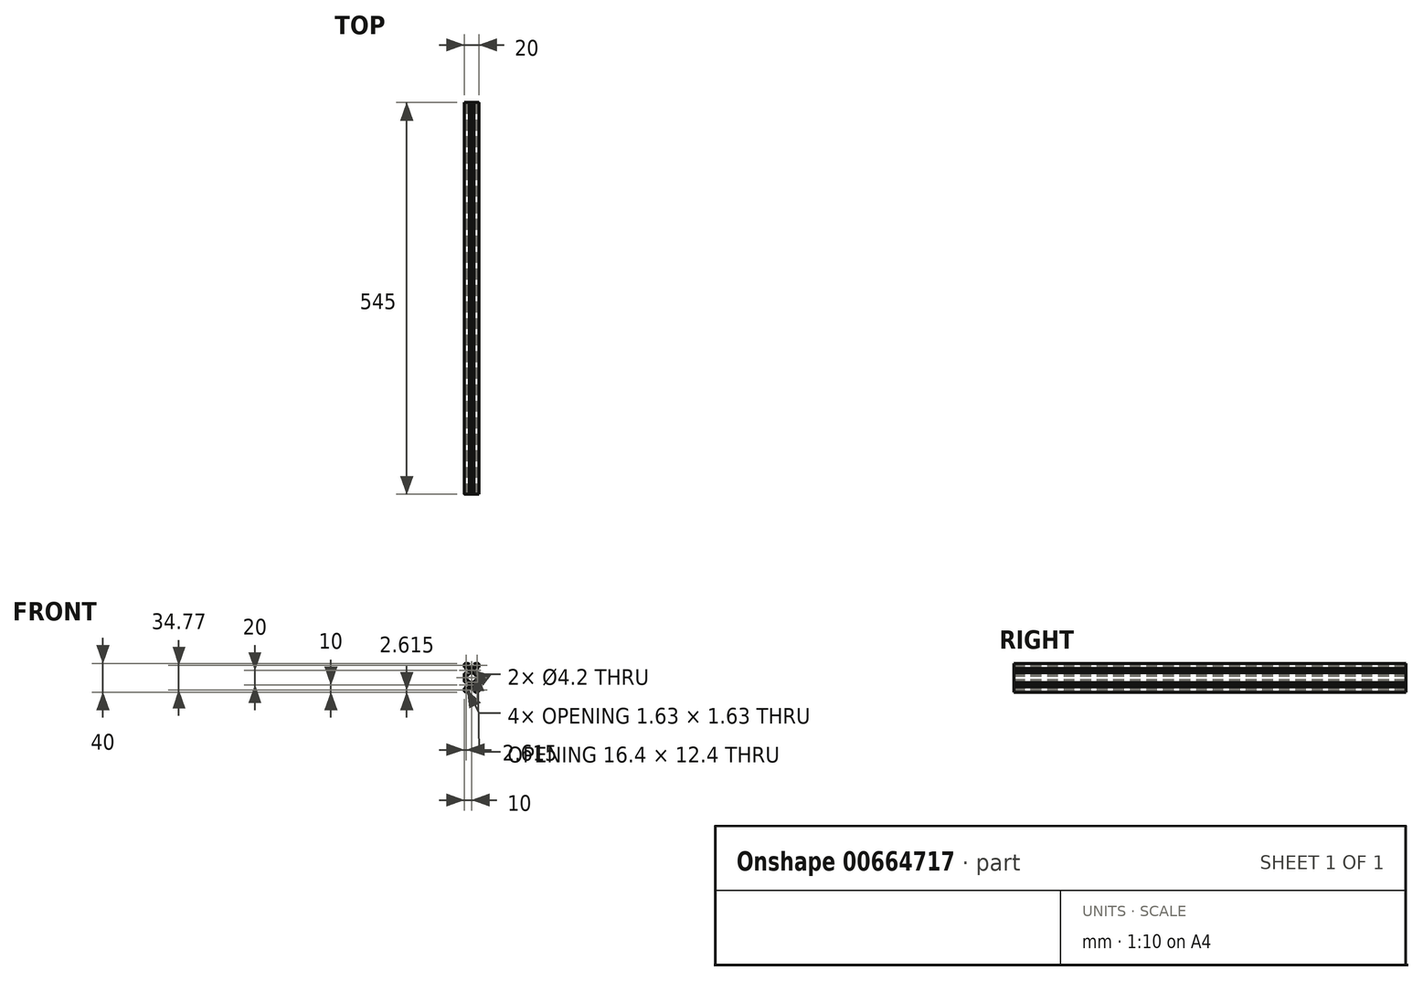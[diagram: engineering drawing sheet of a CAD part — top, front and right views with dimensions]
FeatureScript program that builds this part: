
annotation { "Feature Type Name" : "Feature", "Feature Type Description" : "" }
export const myFeature = defineFeature(function(context is Context, id is Id, definition is map)
    precondition{}
    {
        {
            var Q0;
            Q0=qCreatedBy(makeId("Front.planeOp"),FACE);
            var sketch = newSketch(context, id + "F0", { "sketchPlane" : qUnion([Q0])});
            skLineSegment(sketch, "E0", {"start": v(1.5, 0) * mm, "end": v(5.1, 0) * mm});
            skLineSegment(sketch, "E1", {"start": v(0, -1.5) * mm, "end": v(0, -5.1) * mm});
            skLineSegment(sketch, "E2", {"start": v(5.65, -0.23) * mm, "end": v(7.11, -1.69) * mm});
            skLineSegment(sketch, "E3", {"start": v(7.11, -1.7) * mm, "end": v(7.11, -1.8) * mm});
            skLineSegment(sketch, "E4", {"start": v(0.23, -5.65) * mm, "end": v(1.69, -7.11) * mm});
            skLineSegment(sketch, "E5", {"start": v(1.7, -7.11) * mm, "end": v(1.8, -7.11) * mm});
            skLineSegment(sketch, "E6", {"start": v(1.8, -7.11) * mm, "end": v(1.8, -4.5) * mm});
            skLineSegment(sketch, "E7", {"start": v(1.8, -4.5) * mm, "end": v(3.44, -4.5) * mm});
            skLineSegment(sketch, "E8", {"start": v(7.11, -1.8) * mm, "end": v(4.5, -1.8) * mm});
            skLineSegment(sketch, "E9", {"start": v(4.5, -1.8) * mm, "end": v(4.5, -3.44) * mm});
            skPoint(sketch, "E10.visualSharp", {"position": v(0, 0) * mm});
            skArc(sketch, "E10.filletArc", {"start": v(1.5, 0) * mm, "mid": v(0.44, -0.44) * mm, "end": v(0, -1.5) * mm});
            skPoint(sketch, "E11.visualSharp", {"position": v(5.42, 0) * mm});
            skArc(sketch, "E11.filletArc", {"start": v(5.65, -0.23) * mm, "mid": v(5.4, -0.06) * mm, "end": v(5.1, 0) * mm});
            skPoint(sketch, "E12.visualSharp", {"position": v(0, -5.42) * mm});
            skArc(sketch, "E12.filletArc", {"start": v(0, -5.1) * mm, "mid": v(0.06, -5.4) * mm, "end": v(0.23, -5.65) * mm});
            skLineSegment(sketch, "E13", {"start": v(1.8, -4.5) * mm, "end": v(1.8, 0) * mm, "construction": true});
            skLineSegment(sketch, "E14", {"start": v(4.5, -1.8) * mm, "end": v(0, -1.8) * mm, "construction": true});
            skPoint(sketch, "E15", {"position": v(1.8, -1.8) * mm});
            skLineSegment(sketch, "E16", {"start": v(1.8, -1.8) * mm, "end": v(3.43, -1.8) * mm});
            skLineSegment(sketch, "E17", {"start": v(3.43, -1.8) * mm, "end": v(3.43, -2.34) * mm});
            skLineSegment(sketch, "E18", {"start": v(1.8, -1.8) * mm, "end": v(1.8, -3.43) * mm});
            skLineSegment(sketch, "E19", {"start": v(1.8, -3.43) * mm, "end": v(2.34, -3.43) * mm});
            skLineSegment(sketch, "E20", {"start": v(2.34, -3.43) * mm, "end": v(3.43, -2.34) * mm});
            skArc(sketch, "E21", {"start": v(10, -7.9) * mm, "mid": v(8.52, -8.52) * mm, "end": v(7.9, -10) * mm});
            skLineSegment(sketch, "E22", {"start": v(10, -7.9) * mm, "end": v(10, -6.2) * mm, "construction": true});
            skLineSegment(sketch, "E23", {"start": v(9.9, -6.1) * mm, "end": v(7.16, -6.1) * mm});
            skLineSegment(sketch, "E24", {"start": v(7.16, -6.1) * mm, "end": v(4.5, -3.44) * mm});
            skLineSegment(sketch, "E25", {"start": v(7.9, -10) * mm, "end": v(6.2, -10) * mm, "construction": true});
            skLineSegment(sketch, "E26", {"start": v(6.1, -9.9) * mm, "end": v(6.1, -7.16) * mm});
            skLineSegment(sketch, "E27", {"start": v(6.1, -7.16) * mm, "end": v(3.44, -4.5) * mm});
            skLineSegment(sketch, "E28", {"start": v(1.8, -1.8) * mm, "end": v(10, -10) * mm, "construction": true});
            skLineSegment(sketch, "E29", {"start": v(6.2, -10) * mm, "end": v(6.1, -9.9) * mm});
            skLineSegment(sketch, "E30", {"start": v(10, -6.2) * mm, "end": v(9.9, -6.1) * mm});
            skArc(sketch, "E31", {"start": v(7.9, -10) * mm, "mid": v(8.52, -11.48) * mm, "end": v(10, -12.1) * mm});
            skLineSegment(sketch, "E32", {"start": v(6.2, -10) * mm, "end": v(6.1, -10.1) * mm});
            skLineSegment(sketch, "E33", {"start": v(6.1, -10.1) * mm, "end": v(6.1, -12.84) * mm});
            skLineSegment(sketch, "E34", {"start": v(10, -12.1) * mm, "end": v(10, -13.8) * mm, "construction": true});
            skLineSegment(sketch, "E35", {"start": v(10, -13.8) * mm, "end": v(9.9, -13.9) * mm});
            skLineSegment(sketch, "E36", {"start": v(9.9, -13.9) * mm, "end": v(7.16, -13.9) * mm});
            skLineSegment(sketch, "E37", {"start": v(6.1, -12.84) * mm, "end": v(7.16, -13.9) * mm, "construction": true});
            skLineSegment(sketch, "E38", {"start": v(7.16, -6.1) * mm, "end": v(6.1, -7.16) * mm, "construction": true});
            skLineSegment(sketch, "E39", {"start": v(6.1, -12.84) * mm, "end": v(3.44, -15.5) * mm});
            skLineSegment(sketch, "E40", {"start": v(7.16, -13.9) * mm, "end": v(3.76, -17.3) * mm});
            skLineSegment(sketch, "E41", {"start": v(10, -10) * mm, "end": v(1.8, -18.2) * mm, "construction": true});
            skLineSegment(sketch, "E42", {"start": v(3.44, -15.5) * mm, "end": v(1.8, -15.5) * mm});
            skLineSegment(sketch, "E43", {"start": v(1.8, -15.5) * mm, "end": v(1.8, -12.89) * mm});
            skLineSegment(sketch, "E44", {"start": v(1.8, -12.89) * mm, "end": v(1.7, -12.89) * mm});
            skLineSegment(sketch, "E45", {"start": v(1.7, -12.89) * mm, "end": v(0.23, -14.35) * mm});
            skLineSegment(sketch, "E46", {"start": v(0, -14.9) * mm, "end": v(0, -20) * mm});
            skLineSegment(sketch, "E47", {"start": v(0, -20) * mm, "end": v(1.8, -20) * mm, "construction": true});
            skLineSegment(sketch, "E48", {"start": v(1.8, -20) * mm, "end": v(1.8, -17.3) * mm});
            skLineSegment(sketch, "E49", {"start": v(1.8, -17.3) * mm, "end": v(3.76, -17.3) * mm});
            skPoint(sketch, "E50.visualSharp", {"position": v(0, -14.58) * mm});
            skArc(sketch, "E50.filletArc", {"start": v(0.23, -14.35) * mm, "mid": v(0.06, -14.6) * mm, "end": v(0, -14.9) * mm});
            skLineSegment(sketch, "E51.MirrorCS", {"start": v(13.8, -10) * mm, "end": v(13.9, -10.1) * mm});
            skLineSegment(sketch, "E52.MirrorCS", {"start": v(13.8, -10) * mm, "end": v(13.9, -9.9) * mm});
            skLineSegment(sketch, "E53.MirrorCS", {"start": v(12.9, -1.69) * mm, "end": v(12.9, -1.8) * mm});
            skLineSegment(sketch, "E54.MirrorCS", {"start": v(16.57, -1.8) * mm, "end": v(16.57, -2.34) * mm});
            skLineSegment(sketch, "E55.MirrorCS", {"start": v(10, -13.8) * mm, "end": v(10.1, -13.9) * mm});
            skLineSegment(sketch, "E56.MirrorCS", {"start": v(12.84, -6.1) * mm, "end": v(13.9, -7.16) * mm, "construction": true});
            skArc(sketch, "E57.MirrorCS", {"start": v(14.35, -0.23) * mm, "mid": v(14.6, -0.06) * mm, "end": v(14.9, 0) * mm});
            skArc(sketch, "E58.MirrorCS", {"start": v(20, -5.1) * mm, "mid": v(19.94, -5.4) * mm, "end": v(19.77, -5.65) * mm});
            skLineSegment(sketch, "E59.MirrorCS", {"start": v(13.9, -12.84) * mm, "end": v(12.84, -13.9) * mm, "construction": true});
            skArc(sketch, "E60.MirrorCS", {"start": v(19.77, -14.35) * mm, "mid": v(19.94, -14.6) * mm, "end": v(20, -14.9) * mm});
            skLineSegment(sketch, "E61.MirrorCS", {"start": v(18.31, -7.11) * mm, "end": v(18.2, -7.11) * mm});
            skLineSegment(sketch, "E62.MirrorCS", {"start": v(10, -6.2) * mm, "end": v(10.1, -6.1) * mm});
            skLineSegment(sketch, "E63.MirrorCS", {"start": v(18.2, -3.43) * mm, "end": v(17.66, -3.43) * mm});
            skLineSegment(sketch, "E64.MirrorCS", {"start": v(18.2, -12.89) * mm, "end": v(18.31, -12.89) * mm});
            skLineSegment(sketch, "E65.MirrorCS", {"start": v(17.66, -3.43) * mm, "end": v(16.57, -2.34) * mm});
            skLineSegment(sketch, "E66.MirrorCS", {"start": v(18.31, -12.89) * mm, "end": v(19.77, -14.35) * mm});
            skLineSegment(sketch, "E67.MirrorCS", {"start": v(18.2, -1.8) * mm, "end": v(16.57, -1.8) * mm});
            skArc(sketch, "E68.MirrorCS", {"start": v(18.5, 0) * mm, "mid": v(19.56, -0.44) * mm, "end": v(20, -1.5) * mm});
            skLineSegment(sketch, "E69.MirrorCS", {"start": v(15.5, -1.8) * mm, "end": v(15.5, -3.44) * mm});
            skLineSegment(sketch, "E70.MirrorCS", {"start": v(12.1, -10) * mm, "end": v(13.8, -10) * mm, "construction": true});
            skLineSegment(sketch, "E71.MirrorCS", {"start": v(18.2, -1.8) * mm, "end": v(18.2, -3.43) * mm});
            skPoint(sketch, "E72.MirrorP", {"position": v(18.2, -1.8) * mm});
            skLineSegment(sketch, "E73.MirrorCS", {"start": v(10.1, -6.1) * mm, "end": v(12.84, -6.1) * mm});
            skLineSegment(sketch, "E74.MirrorCS", {"start": v(20, -20) * mm, "end": v(18.2, -20) * mm, "construction": true});
            skLineSegment(sketch, "E75.MirrorCS", {"start": v(18.2, -7.11) * mm, "end": v(18.2, -4.5) * mm});
            skLineSegment(sketch, "E76.MirrorCS", {"start": v(18.5, 0) * mm, "end": v(14.9, 0) * mm});
            skLineSegment(sketch, "E77.MirrorCS", {"start": v(12.84, -6.1) * mm, "end": v(15.5, -3.44) * mm});
            skArc(sketch, "E78.MirrorCS", {"start": v(12.1, -10) * mm, "mid": v(11.48, -11.48) * mm, "end": v(10, -12.1) * mm});
            skLineSegment(sketch, "E79.MirrorCS", {"start": v(12.84, -13.9) * mm, "end": v(16.24, -17.3) * mm});
            skLineSegment(sketch, "E80.MirrorCS", {"start": v(13.9, -7.16) * mm, "end": v(16.56, -4.5) * mm});
            skLineSegment(sketch, "E81.MirrorCS", {"start": v(20, -14.9) * mm, "end": v(20, -20) * mm});
            skLineSegment(sketch, "E82.MirrorCS", {"start": v(13.9, -12.84) * mm, "end": v(16.56, -15.5) * mm});
            skLineSegment(sketch, "E83.MirrorCS", {"start": v(18.2, -20) * mm, "end": v(18.2, -17.3) * mm});
            skLineSegment(sketch, "E84.MirrorCS", {"start": v(14.35, -0.23) * mm, "end": v(12.9, -1.69) * mm});
            skPoint(sketch, "E85.MirrorP", {"position": v(20, 0) * mm});
            skLineSegment(sketch, "E86.MirrorCS", {"start": v(18.2, -4.5) * mm, "end": v(16.56, -4.5) * mm});
            skLineSegment(sketch, "E87.MirrorCS", {"start": v(12.9, -1.8) * mm, "end": v(15.5, -1.8) * mm});
            skPoint(sketch, "E88.MirrorP", {"position": v(20, -14.58) * mm});
            skLineSegment(sketch, "E89.MirrorCS", {"start": v(20, -1.5) * mm, "end": v(20, -5.1) * mm});
            skLineSegment(sketch, "E90.MirrorCS", {"start": v(18.2, -15.5) * mm, "end": v(18.2, -12.89) * mm});
            skLineSegment(sketch, "E91.MirrorCS", {"start": v(16.56, -15.5) * mm, "end": v(18.2, -15.5) * mm});
            skLineSegment(sketch, "E92.MirrorCS", {"start": v(13.9, -9.9) * mm, "end": v(13.9, -7.16) * mm});
            skArc(sketch, "E93.MirrorCS", {"start": v(10, -7.9) * mm, "mid": v(11.48, -8.52) * mm, "end": v(12.1, -10) * mm});
            skPoint(sketch, "E94.MirrorP", {"position": v(14.58, 0) * mm});
            skLineSegment(sketch, "E95.MirrorCS", {"start": v(18.2, -4.5) * mm, "end": v(18.2, 0) * mm, "construction": true});
            skLineSegment(sketch, "E96.MirrorCS", {"start": v(15.5, -1.8) * mm, "end": v(20, -1.8) * mm, "construction": true});
            skLineSegment(sketch, "E97.MirrorCS", {"start": v(10, -10) * mm, "end": v(18.2, -18.2) * mm, "construction": true});
            skLineSegment(sketch, "E98.MirrorCS", {"start": v(18.2, -17.3) * mm, "end": v(16.24, -17.3) * mm});
            skLineSegment(sketch, "E99.MirrorCS", {"start": v(18.2, -1.8) * mm, "end": v(10, -10) * mm, "construction": true});
            skLineSegment(sketch, "E100.MirrorCS", {"start": v(10.1, -13.9) * mm, "end": v(12.84, -13.9) * mm});
            skPoint(sketch, "E101.MirrorP", {"position": v(20, -5.42) * mm});
            skLineSegment(sketch, "E102.MirrorCS", {"start": v(19.77, -5.65) * mm, "end": v(18.31, -7.11) * mm});
            skLineSegment(sketch, "E103.MirrorCS", {"start": v(13.9, -10.1) * mm, "end": v(13.9, -12.84) * mm});
            skLineSegment(sketch, "E104.MirrorCS", {"start": v(6.2, -30) * mm, "end": v(6.1, -29.9) * mm});
            skLineSegment(sketch, "E105.MirrorCS", {"start": v(6.2, -30) * mm, "end": v(6.1, -30.1) * mm});
            skLineSegment(sketch, "E106.MirrorCS", {"start": v(13.8, -30) * mm, "end": v(13.9, -30.1) * mm});
            skLineSegment(sketch, "E107.MirrorCS", {"start": v(13.8, -30) * mm, "end": v(13.9, -29.9) * mm});
            skLineSegment(sketch, "E108.MirrorCS", {"start": v(10, -26.2) * mm, "end": v(9.9, -26.1) * mm});
            skLineSegment(sketch, "E109.MirrorCS", {"start": v(10, -26.2) * mm, "end": v(10.1, -26.1) * mm});
            skArc(sketch, "E110.MirrorCS", {"start": v(14.35, -39.77) * mm, "mid": v(14.6, -39.94) * mm, "end": v(14.9, -40) * mm});
            skLineSegment(sketch, "E111.MirrorCS", {"start": v(10, -33.8) * mm, "end": v(9.9, -33.9) * mm});
            skArc(sketch, "E112.MirrorCS", {"start": v(0.23, -25.65) * mm, "mid": v(0.06, -25.4) * mm, "end": v(0, -25.1) * mm});
            skArc(sketch, "E113.MirrorCS", {"start": v(19.77, -25.65) * mm, "mid": v(19.94, -25.4) * mm, "end": v(20, -25.1) * mm});
            skArc(sketch, "E114.MirrorCS", {"start": v(5.65, -39.77) * mm, "mid": v(5.4, -39.94) * mm, "end": v(5.1, -40) * mm});
            skLineSegment(sketch, "E115.MirrorCS", {"start": v(10, -33.8) * mm, "end": v(10.1, -33.9) * mm});
            skLineSegment(sketch, "E116.MirrorCS", {"start": v(7.11, -38.3) * mm, "end": v(7.11, -38.2) * mm});
            skLineSegment(sketch, "E117.MirrorCS", {"start": v(18.2, -36.57) * mm, "end": v(17.66, -36.57) * mm});
            skArc(sketch, "E118.MirrorCS", {"start": v(0, -34.9) * mm, "mid": v(0.06, -34.6) * mm, "end": v(0.23, -34.35) * mm});
            skLineSegment(sketch, "E119.MirrorCS", {"start": v(1.8, -36.57) * mm, "end": v(2.34, -36.57) * mm});
            skLineSegment(sketch, "E120.MirrorCS", {"start": v(3.43, -38.2) * mm, "end": v(3.43, -37.66) * mm});
            skLineSegment(sketch, "E121.MirrorCS", {"start": v(1.8, -27.11) * mm, "end": v(1.7, -27.11) * mm});
            skLineSegment(sketch, "E122.MirrorCS", {"start": v(18.31, -32.89) * mm, "end": v(18.2, -32.89) * mm});
            skLineSegment(sketch, "E123.MirrorCS", {"start": v(12.9, -38.31) * mm, "end": v(12.9, -38.2) * mm});
            skLineSegment(sketch, "E124.MirrorCS", {"start": v(16.57, -38.2) * mm, "end": v(16.57, -37.66) * mm});
            skLineSegment(sketch, "E125.MirrorCS", {"start": v(10, -27.9) * mm, "end": v(10, -26.2) * mm, "construction": true});
            skLineSegment(sketch, "E126.MirrorCS", {"start": v(1.7, -32.9) * mm, "end": v(1.8, -32.9) * mm});
            skLineSegment(sketch, "E127.MirrorCS", {"start": v(18.2, -27.11) * mm, "end": v(18.31, -27.11) * mm});
            skArc(sketch, "E128.MirrorCS", {"start": v(20, -34.9) * mm, "mid": v(19.94, -34.6) * mm, "end": v(19.77, -34.35) * mm});
            skLineSegment(sketch, "E129.MirrorCS", {"start": v(2.34, -36.57) * mm, "end": v(3.43, -37.66) * mm});
            skLineSegment(sketch, "E130.MirrorCS", {"start": v(13.9, -27.16) * mm, "end": v(12.84, -26.1) * mm, "construction": true});
            skLineSegment(sketch, "E131.MirrorCS", {"start": v(1.8, -38.2) * mm, "end": v(3.43, -38.2) * mm});
            skLineSegment(sketch, "E132.MirrorCS", {"start": v(1.69, -27.11) * mm, "end": v(0.23, -25.65) * mm});
            skLineSegment(sketch, "E133.MirrorCS", {"start": v(17.66, -36.57) * mm, "end": v(16.57, -37.66) * mm});
            skLineSegment(sketch, "E134.MirrorCS", {"start": v(4.5, -38.2) * mm, "end": v(4.5, -36.56) * mm});
            skLineSegment(sketch, "E135.MirrorCS", {"start": v(6.1, -27.16) * mm, "end": v(7.16, -26.1) * mm, "construction": true});
            skLineSegment(sketch, "E136.MirrorCS", {"start": v(1.8, -38.2) * mm, "end": v(1.8, -36.57) * mm});
            skLineSegment(sketch, "E137.MirrorCS", {"start": v(18.2, -38.2) * mm, "end": v(18.2, -36.57) * mm});
            skLineSegment(sketch, "E138.MirrorCS", {"start": v(18.2, -38.2) * mm, "end": v(16.57, -38.2) * mm});
            skPoint(sketch, "E139.MirrorP", {"position": v(20, -40) * mm});
            skLineSegment(sketch, "E140.MirrorCS", {"start": v(18.2, -22.7) * mm, "end": v(16.24, -22.7) * mm});
            skLineSegment(sketch, "E141.MirrorCS", {"start": v(7.16, -26.1) * mm, "end": v(3.76, -22.7) * mm});
            skPoint(sketch, "E142.MirrorP", {"position": v(18.2, -38.2) * mm});
            skPoint(sketch, "E143.MirrorP", {"position": v(14.58, -40) * mm});
            skLineSegment(sketch, "E144.MirrorCS", {"start": v(6.1, -32.84) * mm, "end": v(3.44, -35.5) * mm});
            skArc(sketch, "E145.MirrorCS", {"start": v(18.5, -40) * mm, "mid": v(19.56, -39.56) * mm, "end": v(20, -38.5) * mm});
            skLineSegment(sketch, "E146.MirrorCS", {"start": v(16.56, -24.5) * mm, "end": v(18.2, -24.5) * mm});
            skLineSegment(sketch, "E147.MirrorCS", {"start": v(19.77, -34.35) * mm, "end": v(18.31, -32.89) * mm});
            skLineSegment(sketch, "E148.MirrorCS", {"start": v(18.5, -40) * mm, "end": v(14.9, -40) * mm});
            skArc(sketch, "E149.MirrorCS", {"start": v(12.1, -30) * mm, "mid": v(11.48, -28.52) * mm, "end": v(10, -27.9) * mm});
            skLineSegment(sketch, "E150.MirrorCS", {"start": v(7.16, -33.9) * mm, "end": v(4.5, -36.56) * mm});
            skLineSegment(sketch, "E151.MirrorCS", {"start": v(12.1, -30) * mm, "end": v(13.8, -30) * mm, "construction": true});
            skLineSegment(sketch, "E152.MirrorCS", {"start": v(1.8, -35.5) * mm, "end": v(1.8, -40) * mm, "construction": true});
            skLineSegment(sketch, "E153.MirrorCS", {"start": v(18.2, -38.2) * mm, "end": v(10, -30) * mm, "construction": true});
            skLineSegment(sketch, "E154.MirrorCS", {"start": v(4.5, -38.2) * mm, "end": v(0, -38.2) * mm, "construction": true});
            skLineSegment(sketch, "E155.MirrorCS", {"start": v(10, -30) * mm, "end": v(18.2, -21.8) * mm, "construction": true});
            skLineSegment(sketch, "E156.MirrorCS", {"start": v(15.5, -38.2) * mm, "end": v(15.5, -36.56) * mm});
            skLineSegment(sketch, "E157.MirrorCS", {"start": v(1.5, -40) * mm, "end": v(5.1, -40) * mm});
            skLineSegment(sketch, "E158.MirrorCS", {"start": v(10, -32.1) * mm, "end": v(10, -33.8) * mm, "construction": true});
            skPoint(sketch, "E159.MirrorP", {"position": v(1.8, -38.2) * mm});
            skLineSegment(sketch, "E160.MirrorCS", {"start": v(7.9, -30) * mm, "end": v(6.2, -30) * mm, "construction": true});
            skArc(sketch, "E161.MirrorCS", {"start": v(1.5, -40) * mm, "mid": v(0.44, -39.56) * mm, "end": v(0, -38.5) * mm});
            skLineSegment(sketch, "E162.MirrorCS", {"start": v(12.84, -26.1) * mm, "end": v(16.24, -22.7) * mm});
            skLineSegment(sketch, "E163.MirrorCS", {"start": v(12.9, -38.2) * mm, "end": v(15.5, -38.2) * mm});
            skLineSegment(sketch, "E164.MirrorCS", {"start": v(7.11, -38.2) * mm, "end": v(4.5, -38.2) * mm});
            skLineSegment(sketch, "E165.MirrorCS", {"start": v(1.8, -35.5) * mm, "end": v(3.44, -35.5) * mm});
            skLineSegment(sketch, "E166.MirrorCS", {"start": v(7.16, -33.9) * mm, "end": v(6.1, -32.84) * mm, "construction": true});
            skLineSegment(sketch, "E167.MirrorCS", {"start": v(10.1, -33.9) * mm, "end": v(12.84, -33.9) * mm});
            skLineSegment(sketch, "E168.MirrorCS", {"start": v(13.9, -27.16) * mm, "end": v(16.56, -24.5) * mm});
            skLineSegment(sketch, "E169.MirrorCS", {"start": v(1.8, -38.2) * mm, "end": v(10, -30) * mm, "construction": true});
            skLineSegment(sketch, "E170.MirrorCS", {"start": v(12.84, -33.9) * mm, "end": v(15.5, -36.56) * mm});
            skLineSegment(sketch, "E171.MirrorCS", {"start": v(15.5, -38.2) * mm, "end": v(20, -38.2) * mm, "construction": true});
            skPoint(sketch, "E172.MirrorP", {"position": v(0, -25.42) * mm});
            skLineSegment(sketch, "E173.MirrorCS", {"start": v(18.2, -35.5) * mm, "end": v(18.2, -40) * mm, "construction": true});
            skLineSegment(sketch, "E174.MirrorCS", {"start": v(18.2, -35.5) * mm, "end": v(16.56, -35.5) * mm});
            skLineSegment(sketch, "E175.MirrorCS", {"start": v(18.2, -24.5) * mm, "end": v(18.2, -27.11) * mm});
            skLineSegment(sketch, "E176.MirrorCS", {"start": v(9.9, -33.9) * mm, "end": v(7.16, -33.9) * mm});
            skLineSegment(sketch, "E177.MirrorCS", {"start": v(13.9, -29.9) * mm, "end": v(13.9, -27.16) * mm});
            skLineSegment(sketch, "E178.MirrorCS", {"start": v(20, -38.5) * mm, "end": v(20, -34.9) * mm});
            skLineSegment(sketch, "E179.MirrorCS", {"start": v(13.9, -32.84) * mm, "end": v(16.56, -35.5) * mm});
            skLineSegment(sketch, "E180.MirrorCS", {"start": v(18.2, -20) * mm, "end": v(18.2, -22.7) * mm});
            skArc(sketch, "E181.MirrorCS", {"start": v(10, -32.1) * mm, "mid": v(8.52, -31.48) * mm, "end": v(7.9, -30) * mm});
            skLineSegment(sketch, "E182.MirrorCS", {"start": v(12.84, -33.9) * mm, "end": v(13.9, -32.84) * mm, "construction": true});
            skLineSegment(sketch, "E183.MirrorCS", {"start": v(5.65, -39.77) * mm, "end": v(7.11, -38.31) * mm});
            skLineSegment(sketch, "E184.MirrorCS", {"start": v(10, -30) * mm, "end": v(1.8, -21.8) * mm, "construction": true});
            skLineSegment(sketch, "E185.MirrorCS", {"start": v(20, -25.1) * mm, "end": v(20, -20) * mm});
            skLineSegment(sketch, "E186.MirrorCS", {"start": v(9.9, -26.1) * mm, "end": v(7.16, -26.1) * mm});
            skArc(sketch, "E187.MirrorCS", {"start": v(7.9, -30) * mm, "mid": v(8.52, -28.52) * mm, "end": v(10, -27.9) * mm});
            skLineSegment(sketch, "E188.MirrorCS", {"start": v(18.31, -27.11) * mm, "end": v(19.77, -25.65) * mm});
            skArc(sketch, "E189.MirrorCS", {"start": v(10, -32.1) * mm, "mid": v(11.48, -31.48) * mm, "end": v(12.1, -30) * mm});
            skLineSegment(sketch, "E190.MirrorCS", {"start": v(1.8, -32.9) * mm, "end": v(1.8, -35.5) * mm});
            skLineSegment(sketch, "E191.MirrorCS", {"start": v(1.8, -22.7) * mm, "end": v(3.76, -22.7) * mm});
            skLineSegment(sketch, "E192.MirrorCS", {"start": v(0, -25.1) * mm, "end": v(0, -20) * mm});
            skLineSegment(sketch, "E193.MirrorCS", {"start": v(1.8, -24.5) * mm, "end": v(1.8, -27.11) * mm});
            skLineSegment(sketch, "E194.MirrorCS", {"start": v(14.35, -39.77) * mm, "end": v(12.9, -38.31) * mm});
            skLineSegment(sketch, "E195.MirrorCS", {"start": v(10.1, -26.1) * mm, "end": v(12.84, -26.1) * mm});
            skPoint(sketch, "E196.MirrorP", {"position": v(20, -34.58) * mm});
            skPoint(sketch, "E197.MirrorP", {"position": v(0, -40) * mm});
            skPoint(sketch, "E198.MirrorP", {"position": v(20, -25.42) * mm});
            skLineSegment(sketch, "E199.MirrorCS", {"start": v(0.23, -34.35) * mm, "end": v(1.69, -32.89) * mm});
            skLineSegment(sketch, "E200.MirrorCS", {"start": v(0, -38.5) * mm, "end": v(0, -34.9) * mm});
            skLineSegment(sketch, "E201.MirrorCS", {"start": v(18.2, -32.89) * mm, "end": v(18.2, -35.5) * mm});
            skLineSegment(sketch, "E202.MirrorCS", {"start": v(1.8, -20) * mm, "end": v(1.8, -22.7) * mm});
            skLineSegment(sketch, "E203.MirrorCS", {"start": v(6.1, -29.9) * mm, "end": v(6.1, -27.16) * mm});
            skPoint(sketch, "E204.MirrorP", {"position": v(0, -34.58) * mm});
            skLineSegment(sketch, "E205.MirrorCS", {"start": v(6.1, -27.16) * mm, "end": v(3.44, -24.5) * mm});
            skLineSegment(sketch, "E206.MirrorCS", {"start": v(3.44, -24.5) * mm, "end": v(1.8, -24.5) * mm});
            skPoint(sketch, "E207.MirrorP", {"position": v(5.42, -40) * mm});
            skLineSegment(sketch, "E208.MirrorCS", {"start": v(6.1, -30.1) * mm, "end": v(6.1, -32.84) * mm});
            skLineSegment(sketch, "E209.MirrorCS", {"start": v(13.9, -30.1) * mm, "end": v(13.9, -32.84) * mm});
            skSolve(sketch);
        }
        {
            assignVariable(context, id + "F1", {"name" : "L", "anyValue" : 545 * mm});
        }
        {
            var Q0;
            Q0=qSketchRegion(id+"F0",true);
            extrude(context, id + "F2", {"entities" : qUnion([Q0]), "depth" : getVariable(context, 'L')});
        }
    });
